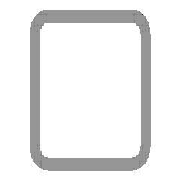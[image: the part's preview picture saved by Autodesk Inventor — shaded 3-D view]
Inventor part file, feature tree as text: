
AUTODESK INVENTOR PART (.ipt)
format: ipt  version: 2022 (Build 260153000, 153)  size: 152,576 bytes
history: native  units: mm (DEFAULTED — no unit token found)
features: other x4, plane x3, sketch x3, split x2
ambient origin geometry x8: Origin, YZ Plane, XZ Plane, XY Plane, X Axis, Y Axis, Z Axis, Center Point
bodies: Solid1 (feature_tree), Body (feature_tree)
feature tree (12):
  parser-record x1  (decoder bookkeeping rows leaked as tree rows — omitted from the tree; the rows remain in map.json)
  other  "Driven Length"
  other  "Start Plane"
  other  "End Plane"
  plane  "Work Plane4"
  split  "Split1"
  plane  "Work Plane5"
  split  "Split2"
  sketch  "Sketch"  dims[d7=4.0mm d9=40.0mm d11=40.0mm d12=2.0mm d13=-5.182521mm d14=320.0mm d15=20.0mm d16=20.0mm d17=90.0deg d18=325.182521mm]
  sketch  "Sketch3"  dims[d3=325.182521mm]
  plane  "Work Plane3"
  sketch  "Sketch4"  dims[d4=0.0mm]
